# Revit family: Domotics-DomesticRanges-GEWISS-CHORUS_COMMAND-THREE-WAY_SWITCH_1M
name_source: partatom
category: Apparecchi elettrici
revit_build: Autodesk Revit 2016 (Build: 20161004_0715(x64)
units: mm (PartAtom-declared; Revit-internal decimal feet)

## family parameters
Condiviso = Sì
Host = Superficie
Mantenere orientamento annotazione = Sì
Numero OmniClass = 23.80.50.11.14
Punto di calcolo locali = No
Quota connettore circolare = Usa diametro
Taglio con vuoti quando caricato = Sì
Tipo di parte = Normale
Titolo OmniClass = Switches

## types (6) — shared parameters
Breaking capacity: = 1.25 In (200 position changes)
Button key = Neutral
Catalogue = DOMOTICS
Catalogue Range = CHORUS - DOMESTIC RANGE
Category = Three-way switch
Distanza_effettiva_x = 1500 mm  [stored 4.92126 ft]
Electrocod = 0130
Glow Wire Test = 850°C
IDF = 4b5ab15b-2fb9-49d2-be7d-6b1aac5df4cd
IDT = 3d8164bf-c18d-49cb-96c5-98ccc73e12be
Immagine tipo = GW14122.jpg
Insulation resistance = > 5 MOhm
Larghezza pulsante = 23 mm  [stored 0.0754593 ft]
No. Chorus modules = 1
Produttore = GEWISS S.p.A.
Prolonged operation (no.of position changes) = 40.000 at In 250 V ac cosÃ˜=0,6
Prospetto di default = 1219 mm
Resistance at test voltage = 2000 V at 50 Hz for 1 minute
SEO = 3 way switch
Simbolo_ = SIMBOLO COMMUTATORI : COMM
Standard; = EN 60669-1
Technical sheet = https://www.gewiss.com
Terminal grip on cable traction = > 50 N
Terminal tightening capacity flexible cables (mm2) = min. 0,75 - max. 2x4
Terminal tightening capacity rigid cables (mm2) = min. 0,5 - max. 2x2,5
Thermo-pressure with ball = 125
Tipo_ = CHORUS COMMUTATORI 1M_BASE : GW14122 - Titanio
URL = https://www.gewiss.com
Version file RFA = 19.0
Voltage = 250 V ac
Voltage: = 250 V ac
Wiring terminals = With screw
zero-valued in all types: Distanza_x

## per-type parameters (varying)
| type | Colour | Description: | Descrizione | EAN code | Modello | Number of poles |
| GW14121 - Titanium | Titanium | 1P - 10AX | 3-WAY SWITCH 1M 1P 10AX UP-DOWN TITANIUM | 8011564265820 | GW14121 | 1P |
| GW10122 - White | White | 2P - 10AX | 3-WAY SWITCH 1M 2P 10AX SYM.UP-DOWN WH | 8011564811539 | GW10122 | 2P |
| GW14122 - Titanium | Titanium | 2P - 10AX | 3-WAY SWITCH 1M 2P 10AX SYM.UP-DOWN TI. | 8011564811553 | GW14122 | 2P |
| GW10121 - White | White | 1P - 10AX | 3-WAY SWITCH, 1M 1P 10AX UP-DOWN WHITE | 8011564257603 | GW10121 | 1P |
| GW12122 - Black | Black | 2P - 10AX | 3-WAY SWITCH 1M 2P 10AX SYM.UP-DOWN BL. | 8011564811546 | GW12122 | 2P |
| GW12121 - Black | Black | 1P - 10AX | 3-WAY SWITCH, 1M 1P 10AX UP-DOWN BLACK | 8011564267169 | GW12121 | 1P |

note: source unit labels omitted for Thermo-pressure with ball — the stored unit's dimension contradicts the parameter name (converter mislabeling)

note: [stored X ft] marks values corroborated as IEEE doubles in the binary element streams (Revit-internal decimal feet)

## geometry (parser evidence)
native form markers: Sweep x1
no freeform markers — native parametric forms only
